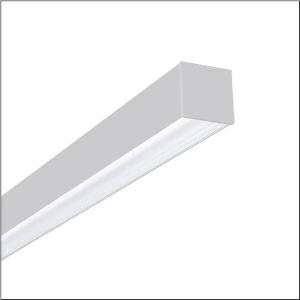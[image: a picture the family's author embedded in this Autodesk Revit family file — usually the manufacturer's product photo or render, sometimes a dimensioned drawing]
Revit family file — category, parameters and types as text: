
# Revit family: silica_r_5mx21bd2w4a_b787
name_source: partatom
category: Lighting Fixtures
units: mm (PartAtom-declared; Revit-internal decimal feet)

## family parameters
Cut with Voids When Loaded = No
Host = Face
Light Source = No
Part Type = Normal
Room Calculation Point = No
Round Connector Dimension = Use Diameter
Shared = No

## types (1)
- --- (1 x LED, 9910 lm, 60.1 W, 4000K)
    Apparent Load = 60 VA
    CIE Flux Codes = 82 97 100 100 100
    Color Rendering = 80
    Color Temperature = 4000K
    Default Elevation = 1800 mm
    Description = Silica®, office luminaire, of aluminium, light emission: direct distribution, primary light characteristic: symmetric, installation type: surface-mounted, LED, rated luminous flux: 9.910lm, luminous efficacy: 165lm/W, light colour: 840, colour temperature: 4000K, control gear: ECG DALI, with terminal, 3+2-pole, max. 2.5mm², mains connection: 230V, AC, 50/60Hz, rated input power: 60W, luminaire housing, of aluminium, traffic white (RAL 9016), length: 2.844mm, width: 65mm, height: 64mm, protection rating (complete): IP20, insulation class (complete): insulation class I (protective earthing), certification: CE, permissible operating ambient temperature: 0..+35°C, standard: EN 50419, packaging unit: 1 piece
    Height = 64 mm
    Lamp = 1 x LED
    Lamp Light Flux = 9910 lm
    Lamp Power = 60.1 W
    Lamp count = 1
    Length = 2845 mm
    Luminous efficacy = 165 lm/W
    Manufacturer = Siteco
    ModVariant = No
    Model = 5MX21BD2W4A
    Mounting Place = Ceiling
    Mounting Type = Surface mounted
    Number of Poles = 1
    OnlyDefault = Yes
    Power Factor = 1
    Product Name = Silica®
    Product group = office luminaire | ceiling mounted
    ProductGroupID = 304
    Protection Class = Protection class I
    Protection Degree = IP 20
    RLX_Detail_Level = 1
    RLX_Emergency_Light_Flux = 0 lm
    RLX_Emergency_Type = 0
    RLX_Emergency_Type_DB = No
    RlxData = <blob elided: 23353 chars, md5=b3c66a93>
    Socket = socket
    Standby Power = 0 W
    System Light Flux = 9910 lm
    System Power = 60 W
    Type Comments = factory setting: luminous flux: 100 % | dim-lin: 254 | 336 mA
    Type Image = l_1003937.jpg
    URL = http://relux.com
    VarID = @adj_138680
    Voltage = 0 V
    Weight = 0.00 kg
    Width = 66 mm

## geometry (parser evidence)
native form markers: Blend x4, Sweep x10
no freeform markers — native parametric forms only
